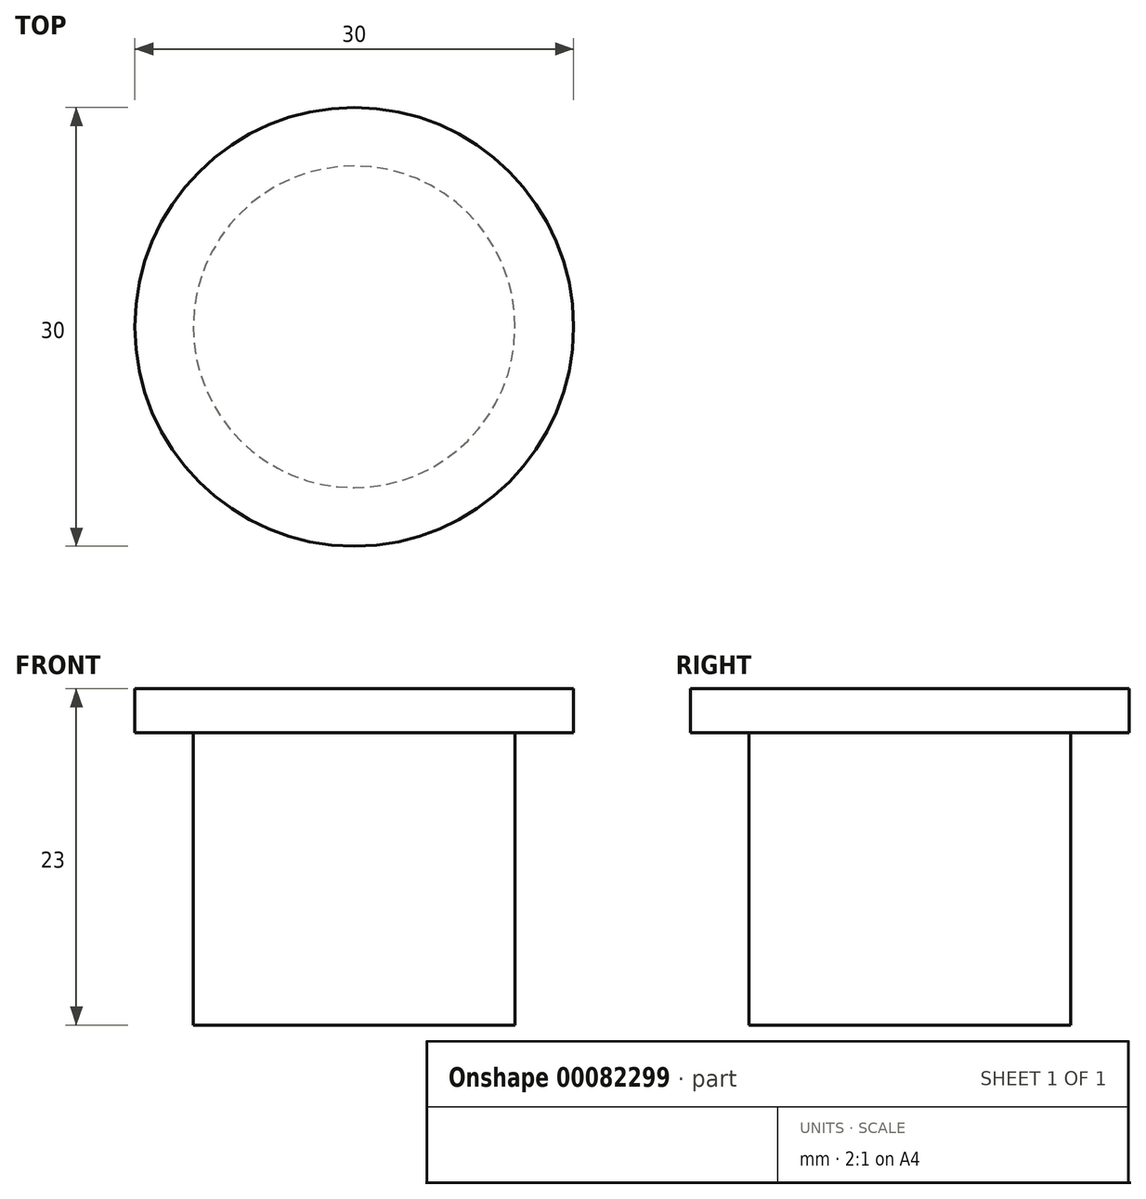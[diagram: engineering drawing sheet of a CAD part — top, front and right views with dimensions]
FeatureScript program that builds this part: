
annotation { "Feature Type Name" : "Feature", "Feature Type Description" : "" }
export const myFeature = defineFeature(function(context is Context, id is Id, definition is map)
    precondition{}
    {
        {
            var Q0;
            Q0=qCreatedBy(makeId("Top.planeOp"),FACE);
            var sketch = newSketch(context, id + "F0", { "sketchPlane" : qUnion([Q0])});
            skCircle(sketch, "E0", {"center": v(-53.66, 0) * mm, "radius": 11 * mm});
            skSolve(sketch);
        }
        {
            var Q0;
            Q0=makeQuery(id+"F0.imprint","IMPRINT",FACE,{"disambiguationData":[TD([[makeQuery(id+"F0.imprint","IMPRINT",EDGE,{"derivedFrom":sQuery(id+"F0.wireOp",EDGE,"E0")}),1.0]])]});
            extrude(context, id + "F1", {"entities" : qUnion([Q0]), "depth" : 20 * mm, "offsetDistance" : 25 * mm});
        }
        {
            var Q0;
            Q0=makeQuery(id+"F1.opExtrude","CAP_FACE",FACE,{"disambiguationData":[OSD([sQuery(id+"F0.wireOp",EDGE,"E0")])],"isStart":false});
            var sketch = newSketch(context, id + "F2", { "sketchPlane" : qUnion([Q0])});
            skCircle(sketch, "E1", {"center": v(-53.66, 0) * mm, "radius": 15 * mm});
            skSolve(sketch);
        }
        {
            var Q0;
            Q0=makeQuery(id+"F2.imprint","IMPRINT",FACE,{"disambiguationData":[TD([[makeQuery(id+"F2.imprint","IMPRINT",EDGE,{"derivedFrom":sQuery(id+"F2.wireOp",EDGE,"E1")}),1.0]])]});
            var Q1;
            Q1=makeQuery(id+"F2.imprint","IMPRINT",FACE,{"disambiguationData":[TD([[makeQuery(id+"F2.imprint","IMPRINT",EDGE,{"derivedFrom":makeQuery(id+"F1.opExtrude","CAP_EDGE",EDGE,{"disambiguationData":[OSD([sQuery(id+"F0.wireOp",EDGE,"E0")])],"isStart":false})}),1.0]])]});
            extrude(context, id + "F3", {"entities" : qUnion([Q0, Q1]), "operationType" : NewBodyOperationType.ADD, "depth" : 3 * mm, "offsetDistance" : 25 * mm});
        }
    });
